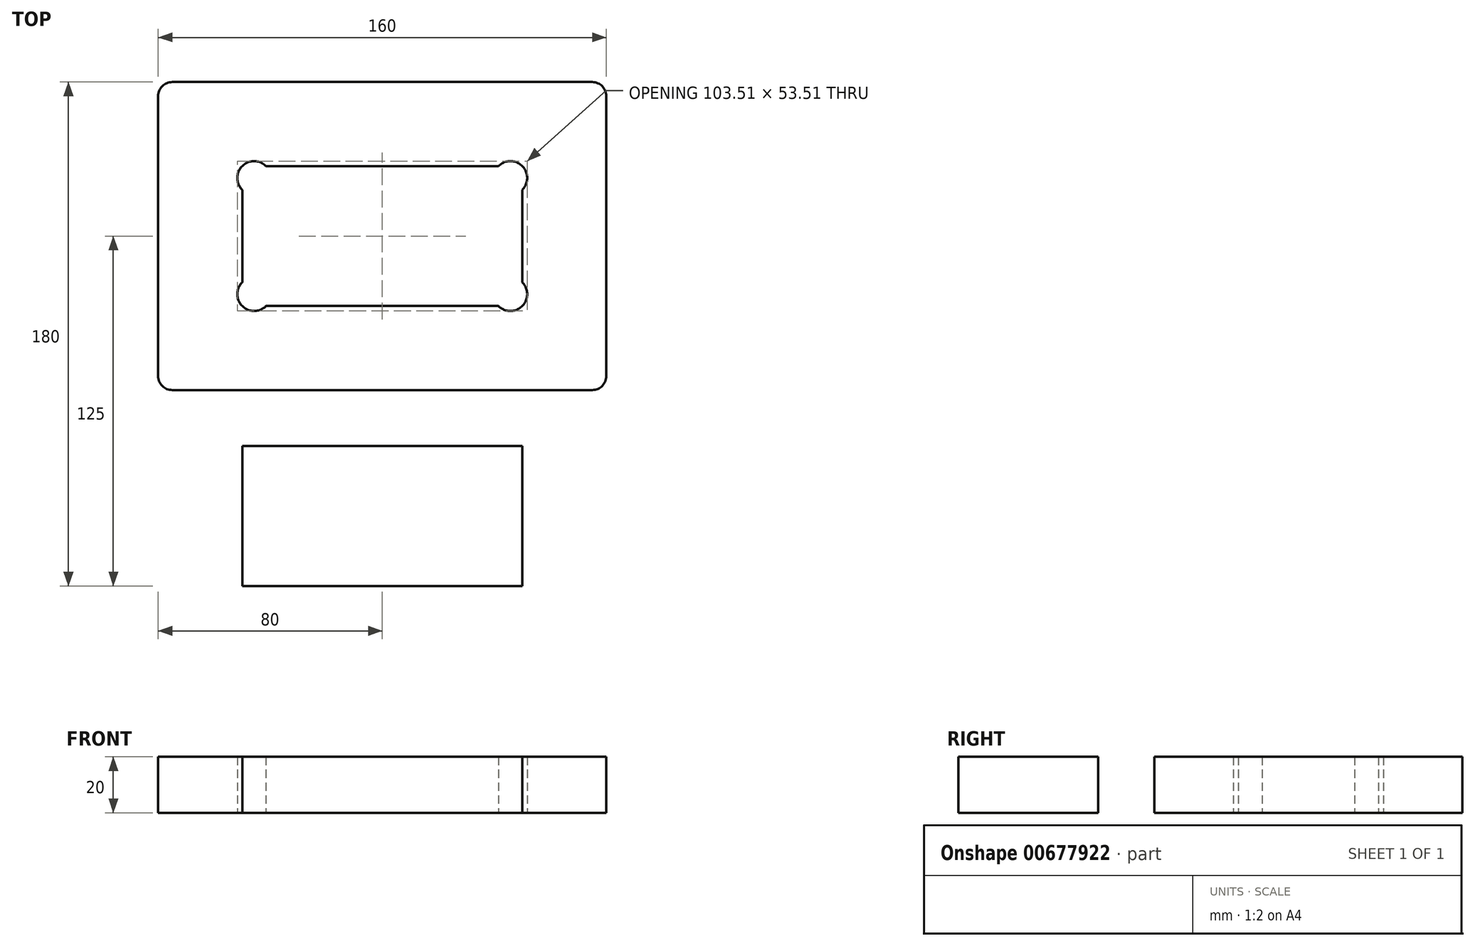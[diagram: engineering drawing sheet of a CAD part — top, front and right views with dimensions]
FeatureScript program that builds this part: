
annotation { "Feature Type Name" : "Feature", "Feature Type Description" : "" }
export const myFeature = defineFeature(function(context is Context, id is Id, definition is map)
    precondition{}
    {
        {
            var Q0;
            Q0=qCreatedBy(makeId("Top.planeOp"),FACE);
            var sketch = newSketch(context, id + "F0", { "sketchPlane" : qUnion([Q0])});
            skLineSegment(sketch, "E0.bottom", {"start": v(-75, 55) * mm, "end": v(75, 55) * mm});
            skLineSegment(sketch, "E0.top", {"start": v(-75, -55) * mm, "end": v(75, -55) * mm});
            skLineSegment(sketch, "E0.left", {"start": v(-80, 50) * mm, "end": v(-80, -50) * mm});
            skLineSegment(sketch, "E0.right", {"start": v(80, 50) * mm, "end": v(80, -50) * mm});
            skPoint(sketch, "E0.middle", {"position": v(0, 0) * mm});
            skLineSegment(sketch, "E1.bottom", {"start": v(-41.51, 25) * mm, "end": v(41.51, 25) * mm});
            skLineSegment(sketch, "E1.top", {"start": v(-41.51, -25) * mm, "end": v(41.51, -25) * mm});
            skLineSegment(sketch, "E1.left", {"start": v(-50, 16.51) * mm, "end": v(-50, -16.51) * mm});
            skLineSegment(sketch, "E1.right", {"start": v(50, 16.51) * mm, "end": v(50, -16.51) * mm});
            skLineSegment(sketch, "E2.bottom", {"start": v(-45.76, 20.76) * mm, "end": v(45.76, 20.76) * mm, "construction": true});
            skLineSegment(sketch, "E2.top", {"start": v(-45.76, -20.76) * mm, "end": v(45.76, -20.76) * mm, "construction": true});
            skLineSegment(sketch, "E2.left", {"start": v(-45.76, 20.76) * mm, "end": v(-45.76, -20.76) * mm, "construction": true});
            skLineSegment(sketch, "E2.right", {"start": v(45.76, 20.76) * mm, "end": v(45.76, -20.76) * mm, "construction": true});
            skArc(sketch, "E3", {"start": v(50, 16.51) * mm, "mid": v(50, 25) * mm, "end": v(41.51, 25) * mm});
            skArc(sketch, "E4", {"start": v(41.51, -25) * mm, "mid": v(50, -25) * mm, "end": v(50, -16.51) * mm});
            skArc(sketch, "E5", {"start": v(-50, -16.51) * mm, "mid": v(-50, -25) * mm, "end": v(-41.51, -25) * mm});
            skLineSegment(sketch, "E6", {"start": v(-50, 25) * mm, "end": v(-45.76, 20.76) * mm, "construction": true});
            skArc(sketch, "E7", {"start": v(-41.51, 25) * mm, "mid": v(-50, 25) * mm, "end": v(-50, 16.51) * mm});
            skPoint(sketch, "E8.orphan", {"position": v(50, -25) * mm});
            skPoint(sketch, "E9.orphan", {"position": v(-50, -25) * mm});
            skPoint(sketch, "E10.orphan", {"position": v(50, 25) * mm});
            skPoint(sketch, "E11.visualSharp", {"position": v(-80, 55) * mm});
            skArc(sketch, "E11.filletArc", {"start": v(-75, 55) * mm, "mid": v(-78.54, 53.54) * mm, "end": v(-80, 50) * mm});
            skPoint(sketch, "E12.visualSharp", {"position": v(80, 55) * mm});
            skArc(sketch, "E12.filletArc", {"start": v(80, 50) * mm, "mid": v(78.54, 53.54) * mm, "end": v(75, 55) * mm});
            skPoint(sketch, "E13.visualSharp", {"position": v(80, -55) * mm});
            skArc(sketch, "E13.filletArc", {"start": v(75, -55) * mm, "mid": v(78.54, -53.54) * mm, "end": v(80, -50) * mm});
            skPoint(sketch, "E14.visualSharp", {"position": v(-80, -55) * mm});
            skArc(sketch, "E14.filletArc", {"start": v(-80, -50) * mm, "mid": v(-78.54, -53.54) * mm, "end": v(-75, -55) * mm});
            skLineSegment(sketch, "E15.bottom", {"start": v(-50, -75) * mm, "end": v(50, -75) * mm});
            skLineSegment(sketch, "E15.top", {"start": v(-50, -125) * mm, "end": v(50, -125) * mm});
            skLineSegment(sketch, "E15.left", {"start": v(-50, -75) * mm, "end": v(-50, -125) * mm});
            skLineSegment(sketch, "E15.right", {"start": v(50, -75) * mm, "end": v(50, -125) * mm});
            skPoint(sketch, "E15.middle", {"position": v(0, -100) * mm});
            skSolve(sketch);
        }
        {
            var Q0;
            Q0 = qSketchRegion(id + "F0", true);
            extrude(context, id + "F1", {"entities" : qUnion([Q0]), "depth" : 20 * mm, "offsetDistance" : 25 * mm});
        }
    });
